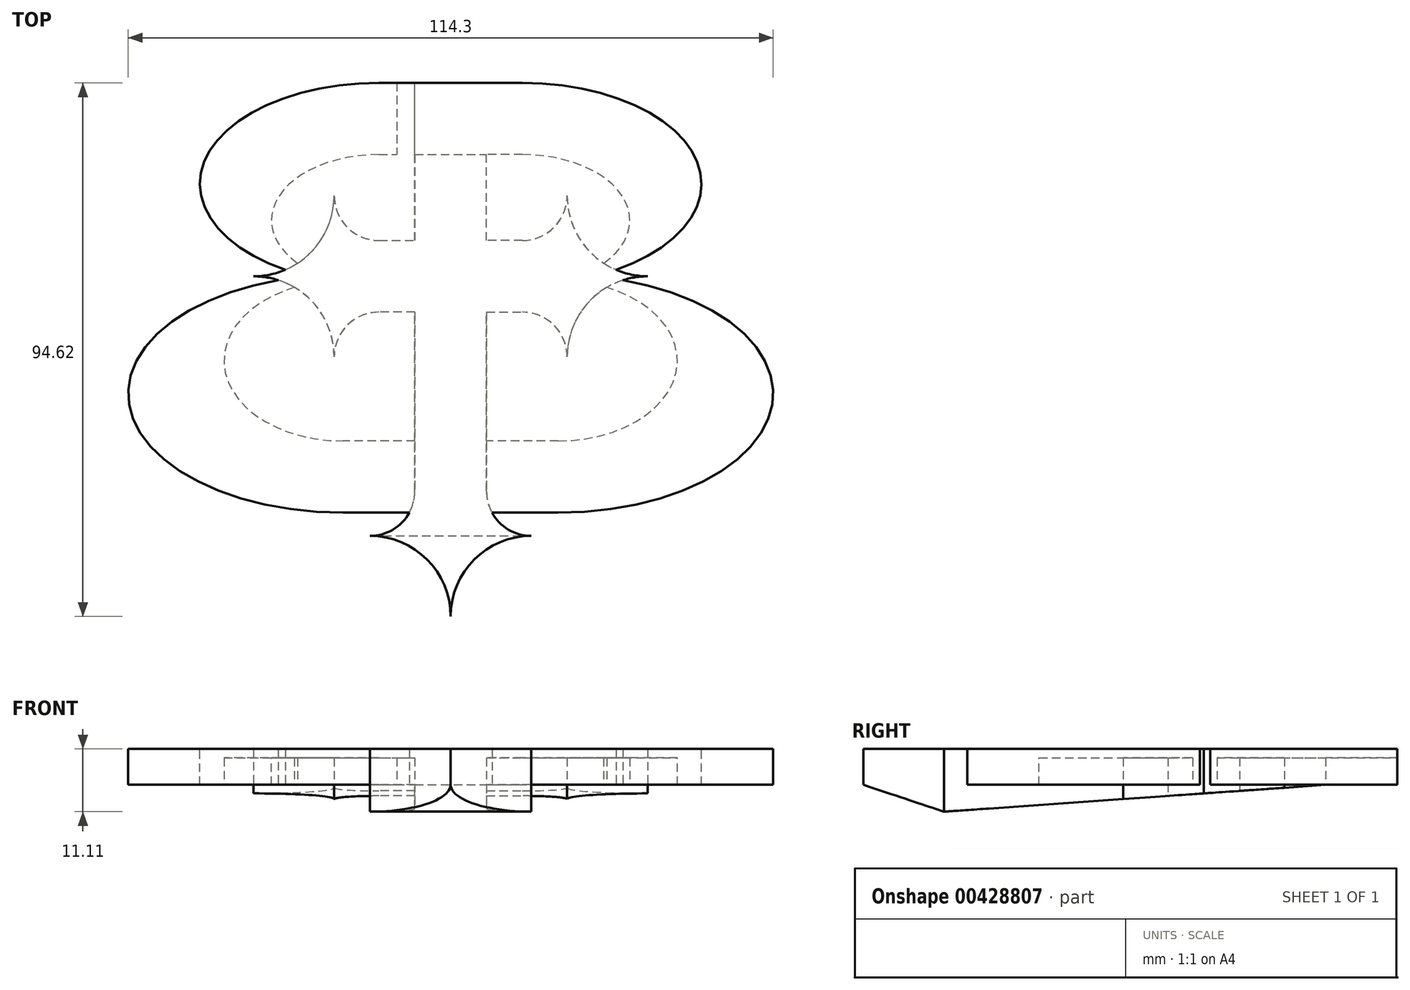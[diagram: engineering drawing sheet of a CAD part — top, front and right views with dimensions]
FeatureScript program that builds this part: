
annotation { "Feature Type Name" : "Feature", "Feature Type Description" : "" }
export const myFeature = defineFeature(function(context is Context, id is Id, definition is map)
    precondition{}
    {
        {
            var Q0;
            Q0=qCreatedBy(makeId("Top.planeOp"),FACE);
            var sketch = newSketch(context, id + "F0", { "sketchPlane" : qUnion([Q0])});
            skEllipticalArc(sketch, "E0", {});
            skEllipticalArc(sketch, "E1", {});
            skLineSegment(sketch, "E2", {"start": v(-12.7, 76.2) * mm, "end": v(12.7, 76.2) * mm});
            skLineSegment(sketch, "E3", {"start": v(0, 0) * mm, "end": v(0, 76.2) * mm, "construction": true});
            skEllipticalArc(sketch, "E4.MirrorCS", {});
            skLineSegment(sketch, "E5", {"start": v(-19.05, 0) * mm, "end": v(19.05, 0) * mm});
            skLineSegment(sketch, "E6", {"start": v(-12.7, 58.3) * mm, "end": v(-44.45, 58.3) * mm, "construction": true});
            skLineSegment(sketch, "E7", {"start": v(-19.05, 21.1) * mm, "end": v(-57.15, 21.1) * mm, "construction": true});
            skLineSegment(sketch, "E8", {"start": v(-12.7, 76.2) * mm, "end": v(-12.7, 58.3) * mm, "construction": true});
            skLineSegment(sketch, "E9", {"start": v(-19.05, 21.1) * mm, "end": v(-19.05, 0) * mm, "construction": true});
            skEllipticalArc(sketch, "E10.MirrorCS", {});
            const initialGuessF0  = {"E0": [-0.0127, 0.058308150725044694, 1, 0, 0.03175, 0.017891849274955303, 1.5707963267948966, 4.300872134317202], "E1": [-0.01905, 0.021102577741770552, 1, 0, 0.0381, 0.021102577741770552, 1.738244406014586, 4.71238898038469], "E4.MirrorCS": [0.01905, 0.021102577741770552, -1, 0, 0.0381, 0.021102577741770552, 1.5707963267948966, 4.544940901165], "E10.MirrorCS": [0.0127, 0.058308150725044694, -1, 0, 0.03175, 0.017891849274955303, 1.9823131728623846, 4.71238898038469]};
            skSetInitialGuess(sketch, initialGuessF0);
            skSolve(sketch);
        }
        {
            var Q0;
            Q0 = qSketchRegion(id + "F0", true);
            extrude(context, id + "F1", {"entities" : qUnion([Q0]), "depth" : 3.17 * mm, "symmetric" : true});
        }
        {
            var Q0;
            Q0=qCreatedBy(makeId("Top.planeOp"),FACE);
            var sketch = newSketch(context, id + "F2", { "sketchPlane" : qUnion([Q0])});
            skLineSegment(sketch, "E11", {"start": v(0, 0) * mm, "end": v(0, 76.2) * mm, "construction": true});
            skLineSegment(sketch, "E12", {"start": v(-19.05, 12.7) * mm, "end": v(0, 12.7) * mm});
            skLineSegment(sketch, "E13", {"start": v(0, 63.5) * mm, "end": v(-12.7, 63.5) * mm});
            skLineSegment(sketch, "E14", {"start": v(-12.7, 76.2) * mm, "end": v(-12.7, 63.5) * mm, "construction": true});
            skLineSegment(sketch, "E15", {"start": v(-19.05, 12.7) * mm, "end": v(-19.05, 0) * mm, "construction": true});
            skLineSegment(sketch, "E16", {"start": v(-19.05, 26.94) * mm, "end": v(-19.05, 12.7) * mm, "construction": true});
            skLineSegment(sketch, "E17", {"start": v(-20.32, 41.15) * mm, "end": v(0, 41.15) * mm, "construction": true});
            skLineSegment(sketch, "E18", {"start": v(-19.05, 26.94) * mm, "end": v(-40.17, 26.94) * mm, "construction": true});
            skLineSegment(sketch, "E19", {"start": v(-31.75, 51.84) * mm, "end": v(-12.7, 51.84) * mm, "construction": true});
            skLineSegment(sketch, "E20", {"start": v(-12.7, 63.5) * mm, "end": v(-12.7, 51.84) * mm, "construction": true});
            skEllipticalArc(sketch, "E21", {});
            skEllipticalArc(sketch, "E22", {});
            skLineSegment(sketch, "E23", {"start": v(-43.87, 61.71) * mm, "end": v(-56.48, 25.05) * mm, "construction": true});
            skLineSegment(sketch, "E24", {"start": v(-31.34, 54.24) * mm, "end": v(-39.62, 30.15) * mm, "construction": true});
            skLineSegment(sketch, "E25.MirrorCS", {"start": v(0, 63.5) * mm, "end": v(6.35, 63.5) * mm});
            skEllipticalArc(sketch, "E26.MirrorCS", {});
            skEllipticalArc(sketch, "E27.MirrorCS", {});
            skLineSegment(sketch, "E28.MirrorCS", {"start": v(19.05, 12.7) * mm, "end": v(0, 12.7) * mm});
            skEllipticalArc(sketch, "E29.0", {});
            skEllipticalArc(sketch, "E29.1", {});
            skLineSegment(sketch, "E29.2", {"start": v(-12.7, 76.2) * mm, "end": v(6.35, 76.2) * mm});
            skLineSegment(sketch, "E29.3", {"start": v(-19.05, 0) * mm, "end": v(19.05, 0) * mm});
            skEllipticalArc(sketch, "E29.4", {});
            skEllipticalArc(sketch, "E29.5", {});
            skLineSegment(sketch, "E30", {"start": v(6.35, 76.2) * mm, "end": v(6.35, 63.5) * mm});
            skLineSegment(sketch, "E31", {"start": v(9.53, 76.2) * mm, "end": v(9.53, 76.2) * mm});
            skLineSegment(sketch, "E32", {"start": v(9.53, 63.5) * mm, "end": v(9.53, 76.2) * mm});
            skLineSegment(sketch, "E33.trimOffspring", {"start": v(9.53, 76.2) * mm, "end": v(12.7, 76.2) * mm});
            skLineSegment(sketch, "E34.trimOffspring", {"start": v(9.53, 63.5) * mm, "end": v(12.7, 63.5) * mm});
            const initialGuessF2  = {"E21": [-0.01905, 0.026936881142607973, 0, -1, 0.014236881142607974, 0.02112032119579259, 3.2017606114576065, 6.283185307179586], "E22": [-0.0127, 0.05183716491706617, -1, 0, 0.01905, 0.01166283508293382, 4.71238898038469, 1.1592794807274087], "E26.MirrorCS": [0.0127, 0.05183716491706617, 1, 0, 0.01905, 0.01166283508293382, 5.1239058264521775, 1.5707963267948966], "E27.MirrorCS": [0.01905, 0.026936881142607973, 0, -1, 0.014236881142607974, 0.02112032119579259, 6.283185307179586, 3.0814246957219797], "E29.0": [-0.01905, 0.021102577741770552, 1, 0, 0.0381, 0.021102577741770552, 1.738244406014586, 4.71238898038469], "E29.1": [-0.0127, 0.058308150725044694, 1, 0, 0.03175, 0.017891849274955303, 1.5707963267948966, 4.300872134317202], "E29.4": [0.0127, 0.058308150725044694, -1, 0, 0.03175, 0.017891849274955303, 1.9823131728623846, 4.71238898038469], "E29.5": [0.01905, 0.021102577741770552, -1, 0, 0.0381, 0.021102577741770552, 1.5707963267948966, 4.544940901165]};
            skSetInitialGuess(sketch, initialGuessF2);
            skSolve(sketch);
        }
        {
            var Q0;
            Q0 = qSketchRegion(id + "F2", true);
            extrude(context, id + "F3", {"entities" : qUnion([Q0]), "operationType" : NewBodyOperationType.ADD, "depth" : 12.7 * mm, "symmetric" : true});
        }
        {
            var Q0;
            Q0=qCreatedBy(makeId("Top.planeOp"),FACE);
            var sketch = newSketch(context, id + "F4", { "sketchPlane" : qUnion([Q0])});
            skLineSegment(sketch, "E35", {"start": v(6.35, 76.2) * mm, "end": v(6.35, 48.26) * mm});
            skLineSegment(sketch, "E36", {"start": v(0, 0) * mm, "end": v(0, 76.2) * mm, "construction": true});
            skLineSegment(sketch, "E37", {"start": v(6.35, 48.26) * mm, "end": v(12.7, 48.26) * mm});
            skArc(sketch, "E38", {"start": v(12.7, 48.26) * mm, "mid": v(18.31, 50.58) * mm, "end": v(20.64, 56.2) * mm});
            skLineSegment(sketch, "E39", {"start": v(0, 41.91) * mm, "end": v(25.4, 41.91) * mm, "construction": true});
            skArc(sketch, "E40", {"start": v(20.64, 56.2) * mm, "mid": v(24.82, 46.1) * mm, "end": v(34.93, 41.91) * mm});
            skLineSegment(sketch, "E41", {"start": v(20.64, 56.2) * mm, "end": v(20.64, 41.91) * mm, "construction": true});
            skLineSegment(sketch, "E42", {"start": v(6.35, 48.26) * mm, "end": v(0, 48.26) * mm, "construction": true});
            skLineSegment(sketch, "E43", {"start": v(6.35, 48.26) * mm, "end": v(6.35, 41.91) * mm, "construction": true});
            skLineSegment(sketch, "E44.MirrorCS", {"start": v(6.35, 35.56) * mm, "end": v(12.7, 35.56) * mm});
            skArc(sketch, "E45.MirrorCS", {"start": v(12.7, 35.56) * mm, "mid": v(18.31, 33.24) * mm, "end": v(20.64, 27.62) * mm});
            skArc(sketch, "E46.MirrorCS", {"start": v(20.64, 27.62) * mm, "mid": v(24.82, 37.73) * mm, "end": v(34.93, 41.91) * mm});
            skArc(sketch, "E47.1.0.0", {"start": v(38.1, 48.26) * mm, "mid": v(43.71, 50.58) * mm, "end": v(46.04, 56.2) * mm, "construction": true});
            skArc(sketch, "E47.1.0.1", {"start": v(46.04, 56.2) * mm, "mid": v(50.22, 46.1) * mm, "end": v(60.33, 41.91) * mm, "construction": true});
            skArc(sketch, "E47.1.0.2", {"start": v(46.04, 27.62) * mm, "mid": v(50.22, 37.73) * mm, "end": v(60.33, 41.91) * mm, "construction": true});
            skArc(sketch, "E47.1.0.3", {"start": v(38.1, 35.56) * mm, "mid": v(43.71, 33.24) * mm, "end": v(46.04, 27.62) * mm, "construction": true});
            skLineSegment(sketch, "E47.direction1", {"start": v(12.7, 27.62) * mm, "end": v(38.1, 27.62) * mm, "construction": true});
            skArc(sketch, "E48.1.0", {"start": v(-6.35, 3.81) * mm, "mid": v(-8.67, -1.8) * mm, "end": v(-14.29, -4.13) * mm});
            skArc(sketch, "E48.1.1", {"start": v(-14.29, -4.13) * mm, "mid": v(-4.18, -8.31) * mm, "end": v(0, -18.41) * mm});
            skArc(sketch, "E48.1.2", {"start": v(14.29, -4.13) * mm, "mid": v(4.18, -8.31) * mm, "end": v(0, -18.41) * mm});
            skArc(sketch, "E48.1.3", {"start": v(6.35, 3.8) * mm, "mid": v(8.67, -1.8) * mm, "end": v(14.29, -4.13) * mm});
            skPoint(sketch, "E48.center", {"position": v(0, 41.91) * mm});
            skLineSegment(sketch, "E48.anchor1", {"start": v(0, 41.91) * mm, "end": v(38.1, 27.62) * mm, "construction": true});
            skLineSegment(sketch, "E48.anchor2", {"start": v(0, 41.91) * mm, "end": v(-14.29, 3.81) * mm, "construction": true});
            skLineSegment(sketch, "E49", {"start": v(6.35, 35.56) * mm, "end": v(6.35, 3.8) * mm});
            skLineSegment(sketch, "E50.MirrorCS", {"start": v(-6.35, 35.56) * mm, "end": v(-6.35, 3.8) * mm});
            skLineSegment(sketch, "E51.MirrorCS", {"start": v(-6.35, 35.56) * mm, "end": v(-12.7, 35.56) * mm});
            skArc(sketch, "E52.MirrorCS", {"start": v(-12.7, 35.56) * mm, "mid": v(-18.31, 33.24) * mm, "end": v(-20.64, 27.62) * mm});
            skArc(sketch, "E53.MirrorCS", {"start": v(-20.64, 27.62) * mm, "mid": v(-24.82, 37.73) * mm, "end": v(-34.93, 41.91) * mm});
            skArc(sketch, "E54.MirrorCS", {"start": v(-20.64, 56.2) * mm, "mid": v(-24.82, 46.1) * mm, "end": v(-34.93, 41.91) * mm});
            skArc(sketch, "E55.MirrorCS", {"start": v(-12.7, 48.26) * mm, "mid": v(-18.31, 50.58) * mm, "end": v(-20.64, 56.2) * mm});
            skLineSegment(sketch, "E56.MirrorCS", {"start": v(-6.35, 48.26) * mm, "end": v(-12.7, 48.26) * mm});
            skLineSegment(sketch, "E57.MirrorCS", {"start": v(-6.35, 76.2) * mm, "end": v(-6.35, 48.26) * mm});
            skLineSegment(sketch, "E58", {"start": v(-6.35, 76.2) * mm, "end": v(6.35, 76.2) * mm});
            skSolve(sketch);
        }
        {
            var Q0;
            Q0 = qSketchRegion(id + "F4", true);
            extrude(context, id + "F5", {"entities" : qUnion([Q0]), "operationType" : NewBodyOperationType.ADD, "depth" : 22.22 * mm, "symmetric" : true});
        }
        {
            var Q0;
            {var subQ0=sQuery(id+"F2.wireOp",EDGE,"E29.2");var subQ1=sQuery(id+"F2.wireOp",EDGE,"E26.MirrorCS");var subQ2=sQuery(id+"F2.wireOp",EDGE,"E34.trimOffspring");var subQ3=sQuery(id+"F2.wireOp",EDGE,"E29.4");var subQ4=sQuery(id+"F2.wireOp",EDGE,"E32");var subQ5=sQuery(id+"F2.wireOp",EDGE,"E33.trimOffspring");Q0=makeQuery(id+"F5.boolean.opBoolean","SPLIT",FACE,{"disambiguationData":[TD([makeQuery(id+"F1.opExtrude","SWEPT_FACE",FACE,{"disambiguationData":[OSD([sQuery(id+"F0.wireOp",EDGE,"E10.MirrorCS")])]})])],"derivedFrom":makeQuery(id+"F3.opExtrude","CAP_FACE",FACE,{"disambiguationData":[OSD([sQuery(id+"F2.wireOp",EDGE,"E12"),sQuery(id+"F2.wireOp",EDGE,"E13"),sQuery(id+"F2.wireOp",EDGE,"E21"),sQuery(id+"F2.wireOp",EDGE,"E22"),sQuery(id+"F2.wireOp",EDGE,"E25.MirrorCS"),subQ1,sQuery(id+"F2.wireOp",EDGE,"E27.MirrorCS"),sQuery(id+"F2.wireOp",EDGE,"E28.MirrorCS"),sQuery(id+"F2.wireOp",EDGE,"E29.0"),sQuery(id+"F2.wireOp",EDGE,"E29.1"),subQ0,sQuery(id+"F2.wireOp",EDGE,"E29.3"),subQ3,sQuery(id+"F2.wireOp",EDGE,"E29.5"),sQuery(id+"F2.wireOp",EDGE,"E30"),subQ4,subQ5,subQ2])],"isStart":true})});}
            var sketch = newSketch(context, id + "F6", { "sketchPlane" : qUnion([Q0])});
            skLineSegment(sketch, "E59.bottom", {"start": v(9.53, -76.2) * mm, "end": v(6.35, -76.2) * mm});
            skLineSegment(sketch, "E59.top", {"start": v(9.53, -63.5) * mm, "end": v(6.35, -63.5) * mm});
            skLineSegment(sketch, "E59.left", {"start": v(9.53, -76.2) * mm, "end": v(9.53, -63.5) * mm});
            skLineSegment(sketch, "E59.right", {"start": v(6.35, -76.2) * mm, "end": v(6.35, -63.5) * mm});
            skSolve(sketch);
        }
        {
            var Q0;
            Q0 = qSketchRegion(id + "F6", true);
            var Q1;
            Q1=makeQuery(id+"F3.boolean.opBoolean","INTERSECT",VERTEX,{"derivedFrom":[makeQuery(id+"F1.opExtrude","CAP_FACE",FACE,{"disambiguationData":[OSD([sQuery(id+"F0.wireOp",EDGE,"E0"),sQuery(id+"F0.wireOp",EDGE,"E1"),sQuery(id+"F0.wireOp",EDGE,"E2"),sQuery(id+"F0.wireOp",EDGE,"E4.MirrorCS"),sQuery(id+"F0.wireOp",EDGE,"E5"),sQuery(id+"F0.wireOp",EDGE,"E10.MirrorCS")])],"isStart":true}),makeQuery(id+"F3.opExtrude","SWEPT_FACE",FACE,{"disambiguationData":[OSD([sQuery(id+"F2.wireOp",EDGE,"E30")])]})]});
            extrude(context, id + "F7", {"entities" : qUnion([Q0]), "operationType" : NewBodyOperationType.ADD, "endBound" : BoundingType.UP_TO_VERTEX, "oppositeDirection" : true, "endBoundEntityVertex" : qUnion([Q1]), "depth" : 25.4 * mm});
        }
        {
            var Q0;
            {var subQ0=sQuery(id+"F2.wireOp",EDGE,"E22");var subQ1=sQuery(id+"F2.wireOp",EDGE,"E33.trimOffspring");var subQ2=sQuery(id+"F2.wireOp",EDGE,"E25.MirrorCS");var subQ3=sQuery(id+"F2.wireOp",EDGE,"E13");var subQ4=sQuery(id+"F2.wireOp",EDGE,"E29.2");var subQ5=sQuery(id+"F2.wireOp",EDGE,"E29.1");Q0=makeQuery(id+"F5.boolean.opBoolean","SPLIT",FACE,{"disambiguationData":[TD([makeQuery(id+"F1.opExtrude","SWEPT_FACE",FACE,{"disambiguationData":[OSD([sQuery(id+"F0.wireOp",EDGE,"E0")])]})])],"derivedFrom":makeQuery(id+"F3.opExtrude","CAP_FACE",FACE,{"disambiguationData":[OSD([sQuery(id+"F2.wireOp",EDGE,"E12"),subQ3,sQuery(id+"F2.wireOp",EDGE,"E21"),subQ0,subQ2,sQuery(id+"F2.wireOp",EDGE,"E26.MirrorCS"),sQuery(id+"F2.wireOp",EDGE,"E27.MirrorCS"),sQuery(id+"F2.wireOp",EDGE,"E28.MirrorCS"),sQuery(id+"F2.wireOp",EDGE,"E29.0"),subQ5,subQ4,sQuery(id+"F2.wireOp",EDGE,"E29.3"),sQuery(id+"F2.wireOp",EDGE,"E29.4"),sQuery(id+"F2.wireOp",EDGE,"E29.5"),sQuery(id+"F2.wireOp",EDGE,"E30"),sQuery(id+"F2.wireOp",EDGE,"E32"),subQ1,sQuery(id+"F2.wireOp",EDGE,"E34.trimOffspring")])],"isStart":true})});}
            var sketch = newSketch(context, id + "F8", { "sketchPlane" : qUnion([Q0])});
            skLineSegment(sketch, "E60.bottom", {"start": v(-6.35, -76.2) * mm, "end": v(-9.53, -76.2) * mm});
            skLineSegment(sketch, "E60.top", {"start": v(-6.35, -63.5) * mm, "end": v(-9.53, -63.5) * mm});
            skLineSegment(sketch, "E60.left", {"start": v(-6.35, -76.2) * mm, "end": v(-6.35, -63.5) * mm});
            skLineSegment(sketch, "E60.right", {"start": v(-9.53, -76.2) * mm, "end": v(-9.53, -63.5) * mm});
            skSolve(sketch);
        }
        {
            var Q0;
            Q0 = qSketchRegion(id + "F8", true);
            var Q1;
            Q1=makeQuery(id+"F5.boolean.opBoolean","SPLIT",FACE,{"disambiguationData":[TD([makeQuery(id+"F3.opExtrude","SWEPT_FACE",FACE,{"disambiguationData":[OSD([sQuery(id+"F2.wireOp",EDGE,"E22")])]})])],"derivedFrom":makeQuery(id+"F1.opExtrude","CAP_FACE",FACE,{"disambiguationData":[OSD([sQuery(id+"F0.wireOp",EDGE,"E0"),sQuery(id+"F0.wireOp",EDGE,"E1"),sQuery(id+"F0.wireOp",EDGE,"E2"),sQuery(id+"F0.wireOp",EDGE,"E4.MirrorCS"),sQuery(id+"F0.wireOp",EDGE,"E5"),sQuery(id+"F0.wireOp",EDGE,"E10.MirrorCS")])],"isStart":true})});
            extrude(context, id + "F9", {"entities" : qUnion([Q0]), "operationType" : NewBodyOperationType.REMOVE, "endBound" : BoundingType.UP_TO_SURFACE, "oppositeDirection" : true, "endBoundEntityFace" : qUnion([Q1]), "depth" : 25.4 * mm});
        }
        {
            var Q0;
            Q0=qCreatedBy(makeId("Right.planeOp"),FACE);
            var sketch = newSketch(context, id + "F10", { "sketchPlane" : qUnion([Q0])});
            skLineSegment(sketch, "E61", {"start": v(63.5, 6.35) * mm, "end": v(-4.13, 11.11) * mm});
            skLineSegment(sketch, "E62", {"start": v(-4.13, 11.11) * mm, "end": v(-18.41, 6.35) * mm});
            skLineSegment(sketch, "E63", {"start": v(-18.41, 6.35) * mm, "end": v(-18.41, 11.11) * mm});
            skLineSegment(sketch, "E64", {"start": v(-18.41, 11.11) * mm, "end": v(76.2, 11.11) * mm});
            skLineSegment(sketch, "E65", {"start": v(76.2, 0) * mm, "end": v(0, 0) * mm, "construction": true});
            skLineSegment(sketch, "E66.MirrorCS", {"start": v(-18.41, -6.35) * mm, "end": v(-18.41, -11.11) * mm});
            skLineSegment(sketch, "E67.MirrorCS", {"start": v(-18.41, -11.11) * mm, "end": v(76.2, -11.11) * mm});
            skLineSegment(sketch, "E68.MirrorCS", {"start": v(-4.13, -11.11) * mm, "end": v(-18.41, -6.35) * mm});
            skLineSegment(sketch, "E69.MirrorCS", {"start": v(63.5, -6.35) * mm, "end": v(-4.13, -11.11) * mm});
            skLineSegment(sketch, "E70.right", {"start": v(76.2, 6.35) * mm, "end": v(76.2, 11.11) * mm});
            skLineSegment(sketch, "E71.0", {"start": v(63.5, 6.35) * mm, "end": v(76.2, 6.35) * mm});
            skLineSegment(sketch, "E72.MirrorCS", {"start": v(76.2, -6.35) * mm, "end": v(76.2, -11.11) * mm});
            skLineSegment(sketch, "E73.MirrorCS", {"start": v(63.5, -6.35) * mm, "end": v(76.2, -6.35) * mm});
            skSolve(sketch);
        }
        {
            var Q0;
            Q0 = qSketchRegion(id + "F10", true);
            extrude(context, id + "F11", {"entities" : qUnion([Q0]), "operationType" : NewBodyOperationType.REMOVE, "endBound" : BoundingType.THROUGH_ALL, "oppositeDirection" : true, "depth" : 25.4 * mm, "hasSecondDirection" : true, "secondDirectionBound" : BoundingType.THROUGH_ALL, "secondDirectionOppositeDirection" : false, "secondDirectionDepth" : 25.4 * mm});
        }
        {
            var Q0;
            Q0=makeQuery(id+"F7.boolean.opBoolean","MERGE",FACE,{"derivedFrom":[makeQuery(id+"F5.boolean.opBoolean","MERGE",FACE,{"derivedFrom":[makeQuery(id+"F3.boolean.opBoolean","MERGE",FACE,{"derivedFrom":[makeQuery(id+"F1.opExtrude","SWEPT_FACE",FACE,{"disambiguationData":[OSD([sQuery(id+"F0.wireOp",EDGE,"E2")])]}),makeQuery(id+"F3.opExtrude","SWEPT_FACE",FACE,{"disambiguationData":[OSD([sQuery(id+"F2.wireOp",EDGE,"E29.2")])]}),makeQuery(id+"F3.opExtrude","SWEPT_FACE",FACE,{"disambiguationData":[OSD([sQuery(id+"F2.wireOp",EDGE,"E33.trimOffspring")])]})]}),makeQuery(id+"F5.opExtrude","SWEPT_FACE",FACE,{"disambiguationData":[OSD([sQuery(id+"F4.wireOp",EDGE,"E58")])]})]}),makeQuery(id+"F7.opExtrude","SWEPT_FACE",FACE,{"disambiguationData":[OSD([sQuery(id+"F6.wireOp",EDGE,"E59.bottom")])]})]});
            var sketch = newSketch(context, id + "F12", { "sketchPlane" : qUnion([Q0])});
            skLineSegment(sketch, "E74", {"start": v(-12.7, 0) * mm, "end": v(12.7, 0) * mm});
            skLineSegment(sketch, "E75", {"start": v(12.7, 0) * mm, "end": v(12.7, 0) * mm});
            skLineSegment(sketch, "E76", {"start": v(12.7, 0) * mm, "end": v(57.15, 0) * mm});
            skLineSegment(sketch, "E77.1", {"start": v(57.15, -6.35) * mm, "end": v(19.05, -6.35) * mm, "construction": true});
            skLineSegment(sketch, "E78", {"start": v(57.15, 6.35) * mm, "end": v(57.15, -6.35) * mm, "construction": true});
            skLineSegment(sketch, "E79", {"start": v(-12.7, 0) * mm, "end": v(-57.15, 0) * mm});
            skLineSegment(sketch, "E80", {"start": v(57.15, 0) * mm, "end": v(57.15, 6.35) * mm});
            skLineSegment(sketch, "E81", {"start": v(57.15, 6.35) * mm, "end": v(57.15, 11.11) * mm});
            skLineSegment(sketch, "E82", {"start": v(57.15, 11.11) * mm, "end": v(-57.15, 11.11) * mm});
            skLineSegment(sketch, "E83", {"start": v(-57.15, 11.11) * mm, "end": v(-57.15, 0) * mm});
            skSolve(sketch);
        }
        {
            var Q0;
            Q0 = qSketchRegion(id + "F12", true);
            extrude(context, id + "F13", {"entities" : qUnion([Q0]), "operationType" : NewBodyOperationType.REMOVE, "endBound" : BoundingType.THROUGH_ALL, "oppositeDirection" : true, "depth" : 25.4 * mm});
        }
    });
